FCSTD DOCUMENT  (FreeCAD 0.16R6707 (Git))
Label: test
License: All rights reserved
LicenseURL: http://en.wikipedia.org/wiki/All_rights_reserved
objects: Sketcher::SketchObject×1, PartDesign::Revolution×1
note: 3 computed .brp shape members not serialized (recipe doc carries the construction recipe); baked Part::Feature solids carry a one-line shape summary decoded from their .brp

FEATURE [Sketcher::SketchObject] Sketch
  sketch-geometry (12):
    g0: LineSegment StartX=-90.3076 StartY=49.7587 StartZ=0 EndX=110.006 EndY=49.7587 EndZ=0
    g1: LineSegment StartX=110.006 StartY=49.7587 StartZ=0 EndX=110.006 EndY=19.5066 EndZ=0
    g2: LineSegment StartX=110.006 StartY=-29.8041 StartZ=0 EndX=-90.3076 EndY=-29.8041 EndZ=0
    g3: LineSegment StartX=-90.3076 StartY=-29.8041 StartZ=0 EndX=-90.3076 EndY=0.319919 EndZ=0
    g4: LineSegment StartX=-109.751 StartY=19.6347 StartZ=0 EndX=-90.3076 EndY=19.6347 EndZ=0
    g5: LineSegment StartX=-90.3076 StartY=0.319919 StartZ=0 EndX=-109.751 EndY=0.319919 EndZ=0
    g6: LineSegment StartX=-109.751 StartY=0.319919 StartZ=0 EndX=-109.751 EndY=19.6347 EndZ=0
    g7: LineSegment StartX=110.006 StartY=19.5066 StartZ=0 EndX=129.961 EndY=19.5066 EndZ=0
    g8: LineSegment StartX=129.961 StartY=19.5066 StartZ=0 EndX=129.961 EndY=0.191741 EndZ=0
    g9: LineSegment StartX=129.961 StartY=0.191741 StartZ=0 EndX=110.006 EndY=0.191741 EndZ=0
    g10: LineSegment StartX=-90.3076 StartY=19.6347 StartZ=0 EndX=-90.3076 EndY=49.7587 EndZ=0
    g11: LineSegment StartX=110.006 StartY=0.191741 StartZ=0 EndX=110.006 EndY=-29.8041 EndZ=0
  constraints (33):
    c: Coincident(g0,g1)
    c: Coincident(g11,g2)
    c: Coincident(g2,g3)
    c: Coincident(g10,g0)
    c: Horizontal(g0)
    c: Horizontal(g2)
    c: Vertical(g1)
    c: Vertical(g3)
    c: Coincident(g5,g6)
    c: Coincident(g6,g4)
    c: Horizontal(g4)
    c: Horizontal(g5)
    c: Vertical(g6)
    c: Coincident(g7,g8)
    c: Coincident(g8,g9)
    c: Horizontal(g7)
    c: Horizontal(g9)
    c: Vertical(g8)
    c: Coincident(g10,g4)
    c: Tangent(g3,g10)
    c: Coincident(g5,g3)
    c: Coincident(g1,g7)
    c: Coincident(g11,g9)
    c: Tangent(g1,g11)
    c: Parallel(g4,g5)
    c: Equal(g6,g8)
    c: Parallel(g4,g5)
    c: Parallel(g5,g7)
    c: Parallel(g7,g9)
    c: Parallel(g0,g2)
    c: Parallel(g10,g3)
    c: Parallel(g3,g1)
    c: Parallel(g1,g11)
FEATURE [PartDesign::Revolution] Revolution
  Angle = 360
  Axis = (1,0,0)
  Base = (0,0,0)
  ReferenceAxis = -> Sketch [H_Axis]
  Sketch = -> Sketch
